# Revit family: BL-2513-11-PORTARROLLO GENESIS
name_source: partatom
category: Plumbing Fixtures
revit_build: Autodesk Revit 2018 (Build: 20170223_1515(x64)
units: mm (PartAtom-declared; Revit-internal decimal feet)

## family parameters
Cut with Voids When Loaded = No
Host = Face
OmniClass Number = 23.31.11.00
Part Type = Normal
Room Calculation Point = No
Round Connector Dimension = Use Diameter
Shared = No

## types (1)
- BL-2513-11
    Alto = 105 mm  [stored 0.344488 ft]
    Ancho = 181 mm
    CW Connection = Yes
    Default Elevation = 0 mm  [stored 0 ft]
    Description = PORTAROLLO
    Finish = Plastico ABS Cromado
    HW Connection = Yes
    Link Ficha Tecnica = http://infotecnica.gricol.com
    Manufacturer = Gricol
    Model = BL-2513-11
    Product Name = PORTAROLLO GENESIS
    Profundidad = 70 mm
    Type Image = PORTARROLLO GENESIS FOTO.jpg
    URL = https://www.gricol.com
    Vent Connection = No
    Waste Connection = No

note: [stored X ft] marks values corroborated as IEEE doubles in the binary element streams (Revit-internal decimal feet)

## geometry (parser evidence)
native form markers: Blend x4, Sweep x5
no freeform markers — native parametric forms only
